# Revit family: All-Lite _EFJ-645_R17
name_source: partatom
category: Mechanical Equipment
revit_build: Autodesk Revit 2017 (Build: 20160225_1515(x64)
units: mm (PartAtom-declared; Revit-internal decimal feet)

## family parameters
Cut with Voids When Loaded = No
Host = Face
Part Type = Normal
Room Calculation Point = No
Round Connector Dimension = Use Diameter
Shared = No

## types (2) — shared parameters
Air Volume Delivered = 9359 cfm
Assembly Code = B3020300
Blades = 45° x 0.081'' thick J- style.
Default Elevation = 0"
Depth = 6"
Description = The EFJ-645 extruded aluminum louver is designed for intake
and exhaust application where protection against water
infiltration is not critical. The EFJ-645 is well suited for special
shape applications and is available with hidden mullions for a
continuous blade appearance of multiple section assemblies.
The EFJ-645 is available in a wide array of anodized and
painted finishes including custom color matching.
Design Load = 30 psf
Frame = 6'' deep x 0.081'' thick channel.
Free Area Velocity = 1155 fpm
Manufacturer = Pottorff
Material = Mill finish 6063-T5 extruded aluminum.
Maximum Size = 60'' x 120''
Minimum Size = 4.5'' x 9.5'
Model = EFJ-645
Modeled By = Commense Studio
Mullion = Visible
Pressure Loss = .18 in. wg
Screen = 1/2'' x 0.063'' expanded and flattened aluminum.

## per-type parameters (varying)
| type | Array Control 1 | Array Control 2 | Blade Width | Height | Height Control | Product URL | URL | Width | Width Control |
| 60" x 120" | 18 | 18 | 58" | 120" | 120" | https://www.alllite.com | https://www.alllite.com | 60" | 60" |
| 36" x 48" | 6 | 6 | 34" | 48" | 48" |  | https://www.pottorff.com | 36" | 36" |

## geometry (parser evidence)
native form markers: Blend x4, Sweep x6
no freeform markers — native parametric forms only
